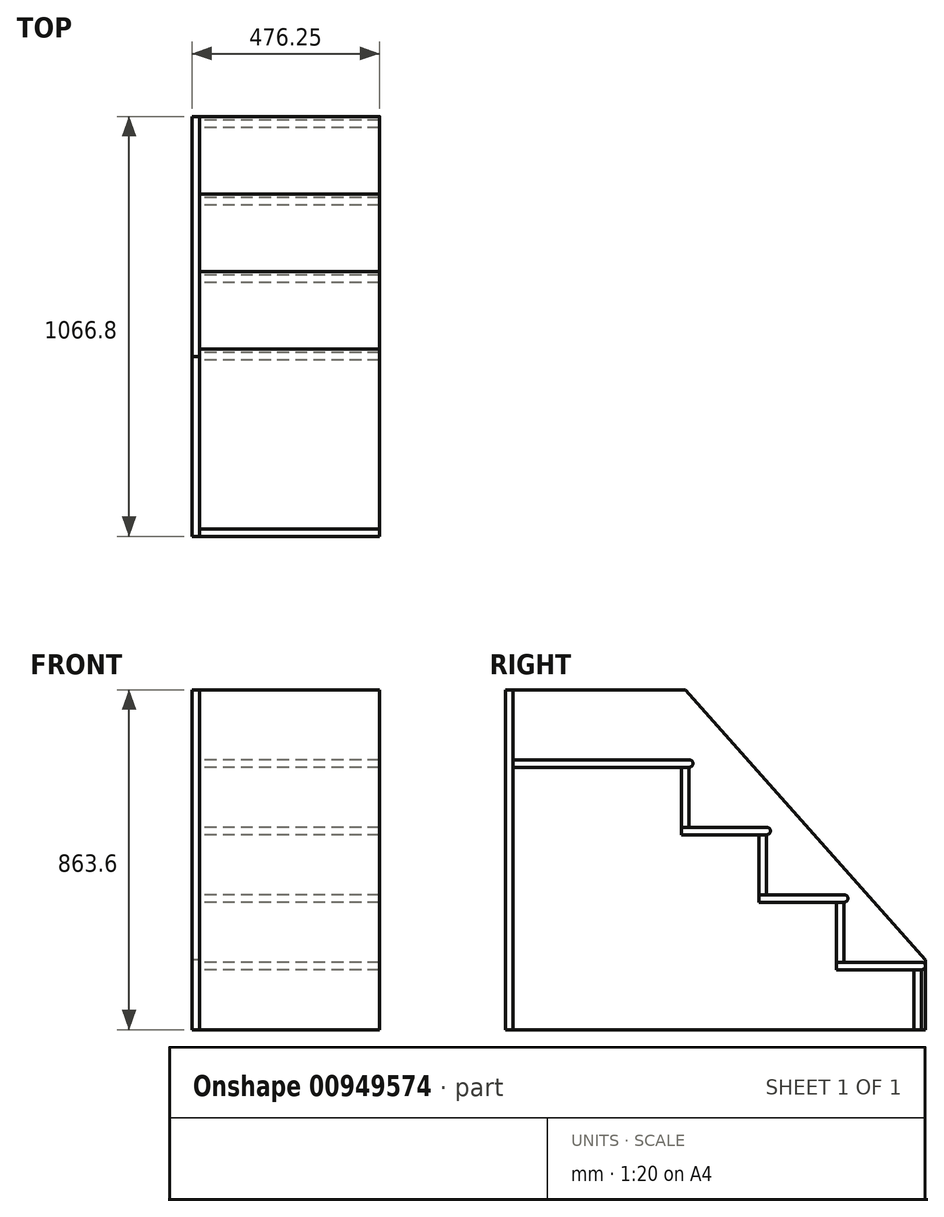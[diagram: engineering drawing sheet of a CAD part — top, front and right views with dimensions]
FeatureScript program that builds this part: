
annotation { "Feature Type Name" : "Feature", "Feature Type Description" : "" }
export const myFeature = defineFeature(function(context is Context, id is Id, definition is map)
    precondition{}
    {
        {
            var Q0;
            Q0=qCreatedBy(makeId("Right.planeOp"),FACE);
            var sketch = newSketch(context, id + "F0", { "sketchPlane" : qUnion([Q0])});
            skLineSegment(sketch, "E0", {"start": v(-1066.8, 863.6) * mm, "end": v(-1066.8, 0) * mm});
            skLineSegment(sketch, "E1", {"start": v(-1066.8, 0) * mm, "end": v(0, 0) * mm});
            skLineSegment(sketch, "E2", {"start": v(0, 0) * mm, "end": v(0, 177.8) * mm});
            skLineSegment(sketch, "E3", {"start": v(0, 177.8) * mm, "end": v(-609.6, 863.6) * mm});
            skLineSegment(sketch, "E4", {"start": v(-609.6, 863.6) * mm, "end": v(-1066.8, 863.6) * mm});
            skSolve(sketch);
        }
        {
            var Q0;
            Q0=makeQuery(id+"F0.imprint","IMPRINT",FACE,{"disambiguationData":[TD([[makeQuery(id+"F0.imprint","IMPRINT",EDGE,{"derivedFrom":sQuery(id+"F0.wireOp",EDGE,"E0")}),1.0]])]});
            extrude(context, id + "F1", {"entities" : qUnion([Q0]), "depth" : 19.05 * mm, "offsetDistance" : 25.4 * mm});
        }
        {
            var Q0;
            Q0=makeQuery(id+"F1.opExtrude","CAP_FACE",FACE,{"disambiguationData":[OSD([sQuery(id+"F0.wireOp",EDGE,"E0"),sQuery(id+"F0.wireOp",EDGE,"E1"),sQuery(id+"F0.wireOp",EDGE,"E2"),sQuery(id+"F0.wireOp",EDGE,"E3"),sQuery(id+"F0.wireOp",EDGE,"E4")])],"isStart":false});
            var sketch = newSketch(context, id + "F2", { "sketchPlane" : qUnion([Q0])});
            skLineSegment(sketch, "E5.bottom", {"start": v(-1047.75, 863.6) * mm, "end": v(-1066.8, 863.6) * mm});
            skLineSegment(sketch, "E5.top", {"start": v(-1047.75, 0) * mm, "end": v(-1066.8, 0) * mm});
            skLineSegment(sketch, "E5.left", {"start": v(-1047.75, 863.6) * mm, "end": v(-1047.75, 0) * mm});
            skLineSegment(sketch, "E5.right", {"start": v(-1066.8, 863.6) * mm, "end": v(-1066.8, 0) * mm});
            skSolve(sketch);
        }
        {
            var Q0;
            Q0 = qSketchRegion(id + "F2", true);
            extrude(context, id + "F3", {"entities" : qUnion([Q0]), "depth" : 457.2 * mm, "offsetDistance" : 25.4 * mm});
        }
        {
            var Q0;
            Q0=makeQuery(id+"F1.opExtrude","CAP_FACE",FACE,{"disambiguationData":[OSD([sQuery(id+"F0.wireOp",EDGE,"E0"),sQuery(id+"F0.wireOp",EDGE,"E1"),sQuery(id+"F0.wireOp",EDGE,"E2"),sQuery(id+"F0.wireOp",EDGE,"E3"),sQuery(id+"F0.wireOp",EDGE,"E4")])],"isStart":false});
            var sketch = newSketch(context, id + "F4", { "sketchPlane" : qUnion([Q0])});
            skLineSegment(sketch, "E6.bottom", {"start": v(-1047.75, 685.8) * mm, "end": v(-590.55, 685.8) * mm});
            skLineSegment(sketch, "E6.top", {"start": v(-1047.75, 666.75) * mm, "end": v(-590.55, 666.75) * mm});
            skLineSegment(sketch, "E6.left", {"start": v(-1047.75, 685.8) * mm, "end": v(-1047.75, 666.75) * mm});
            skLineSegment(sketch, "E6.right", {"start": v(-590.55, 685.8) * mm, "end": v(-590.55, 666.75) * mm});
            skLineSegment(sketch, "E7.bottom", {"start": v(-225.42, 171.45) * mm, "end": v(0, 171.45) * mm});
            skLineSegment(sketch, "E7.top", {"start": v(-225.42, 152.4) * mm, "end": v(0, 152.4) * mm});
            skLineSegment(sketch, "E7.left", {"start": v(-225.42, 171.45) * mm, "end": v(-225.42, 152.4) * mm});
            skLineSegment(sketch, "E7.right", {"start": v(0, 171.45) * mm, "end": v(0, 152.4) * mm});
            skLineSegment(sketch, "E8.bottom", {"start": v(-422.28, 342.9) * mm, "end": v(-196.85, 342.9) * mm});
            skLineSegment(sketch, "E8.top", {"start": v(-422.28, 323.85) * mm, "end": v(-196.85, 323.85) * mm});
            skLineSegment(sketch, "E8.left", {"start": v(-422.28, 342.9) * mm, "end": v(-422.28, 323.85) * mm});
            skLineSegment(sketch, "E8.right", {"start": v(-196.85, 342.9) * mm, "end": v(-196.85, 323.85) * mm});
            skLineSegment(sketch, "E9.bottom", {"start": v(-619.12, 514.35) * mm, "end": v(-393.7, 514.35) * mm});
            skLineSegment(sketch, "E9.top", {"start": v(-619.12, 495.3) * mm, "end": v(-393.7, 495.3) * mm});
            skLineSegment(sketch, "E9.left", {"start": v(-619.12, 514.35) * mm, "end": v(-619.12, 495.3) * mm});
            skLineSegment(sketch, "E9.right", {"start": v(-393.7, 514.35) * mm, "end": v(-393.7, 495.3) * mm});
            skSolve(sketch);
        }
        {
            var Q0;
            Q0 = qSketchRegion(id + "F4", true);
            var Q1;
            Q1=makeQuery(id+"F3.opExtrude","CAP_FACE",FACE,{"disambiguationData":[OSD([sQuery(id+"F2.wireOp",EDGE,"E5.bottom"),sQuery(id+"F2.wireOp",EDGE,"E5.top"),sQuery(id+"F2.wireOp",EDGE,"E5.left"),sQuery(id+"F2.wireOp",EDGE,"E5.right")])],"isStart":false});
            extrude(context, id + "F5", {"entities" : qUnion([Q0]), "endBound" : BoundingType.UP_TO_SURFACE, "depth" : 25.4 * mm, "endBoundEntityFace" : qUnion([Q1]), "offsetDistance" : 25.4 * mm});
        }
        {
            var Q0;
            Q0=makeQuery(id+"F5.opExtrude","SWEPT_EDGE",EDGE,{"disambiguationData":[OSD([sQuery(id+"F4.wireOp",EDGE,"E6.bottom"),sQuery(id+"F4.wireOp",EDGE,"E6.right")])]});
            var Q1;
            Q1=makeQuery(id+"F5.opExtrude","SWEPT_EDGE",EDGE,{"disambiguationData":[OSD([sQuery(id+"F4.wireOp",EDGE,"E6.top"),sQuery(id+"F4.wireOp",EDGE,"E6.right")])]});
            var Q2;
            Q2=makeQuery(id+"F5.opExtrude","SWEPT_EDGE",EDGE,{"disambiguationData":[OSD([sQuery(id+"F4.wireOp",EDGE,"E9.bottom"),sQuery(id+"F4.wireOp",EDGE,"E9.right")])]});
            var Q3;
            Q3=makeQuery(id+"F5.opExtrude","SWEPT_EDGE",EDGE,{"disambiguationData":[OSD([sQuery(id+"F4.wireOp",EDGE,"E9.top"),sQuery(id+"F4.wireOp",EDGE,"E9.right")])]});
            var Q4;
            Q4=makeQuery(id+"F5.opExtrude","SWEPT_EDGE",EDGE,{"disambiguationData":[OSD([sQuery(id+"F4.wireOp",EDGE,"E8.bottom"),sQuery(id+"F4.wireOp",EDGE,"E8.right")])]});
            var Q5;
            Q5=makeQuery(id+"F5.opExtrude","SWEPT_EDGE",EDGE,{"disambiguationData":[OSD([sQuery(id+"F4.wireOp",EDGE,"E8.top"),sQuery(id+"F4.wireOp",EDGE,"E8.right")])]});
            var Q6;
            Q6=makeQuery(id+"F5.opExtrude","SWEPT_EDGE",EDGE,{"disambiguationData":[OSD([sQuery(id+"F0.wireOp",EDGE,"E2"),sQuery(id+"F4.wireOp",EDGE,"E7.bottom"),sQuery(id+"F4.wireOp",EDGE,"E7.right")])]});
            var Q7;
            Q7=makeQuery(id+"F5.opExtrude","SWEPT_EDGE",EDGE,{"disambiguationData":[OSD([sQuery(id+"F0.wireOp",EDGE,"E2"),sQuery(id+"F4.wireOp",EDGE,"E7.top"),sQuery(id+"F4.wireOp",EDGE,"E7.right")])]});
            fillet(context, id + "F6", {"entities" : qUnion([Q0, Q1, Q2, Q3, Q4, Q5, Q6, Q7]), "radius" : 9.52 * mm, "tangentPropagation" : true, "allowEdgeOverflow" : false});
        }
        {
            var Q0;
            Q0=makeQuery(id+"F1.opExtrude","CAP_FACE",FACE,{"disambiguationData":[OSD([sQuery(id+"F0.wireOp",EDGE,"E0"),sQuery(id+"F0.wireOp",EDGE,"E1"),sQuery(id+"F0.wireOp",EDGE,"E2"),sQuery(id+"F0.wireOp",EDGE,"E3"),sQuery(id+"F0.wireOp",EDGE,"E4")])],"isStart":false});
            var sketch = newSketch(context, id + "F7", { "sketchPlane" : qUnion([Q0])});
            skLineSegment(sketch, "E10.bottom", {"start": v(-600.08, 666.75) * mm, "end": v(-619.12, 666.75) * mm});
            skLineSegment(sketch, "E10.top", {"start": v(-600.08, 514.35) * mm, "end": v(-619.12, 514.35) * mm});
            skLineSegment(sketch, "E10.left", {"start": v(-600.08, 666.75) * mm, "end": v(-600.08, 514.35) * mm});
            skLineSegment(sketch, "E10.right", {"start": v(-619.12, 666.75) * mm, "end": v(-619.12, 514.35) * mm});
            skLineSegment(sketch, "E11.bottom", {"start": v(-403.23, 495.3) * mm, "end": v(-422.28, 495.3) * mm});
            skLineSegment(sketch, "E11.top", {"start": v(-403.23, 342.9) * mm, "end": v(-422.28, 342.9) * mm});
            skLineSegment(sketch, "E11.left", {"start": v(-403.23, 495.3) * mm, "end": v(-403.23, 342.9) * mm});
            skLineSegment(sketch, "E11.right", {"start": v(-422.28, 495.3) * mm, "end": v(-422.28, 342.9) * mm});
            skLineSegment(sketch, "E12.bottom", {"start": v(-206.38, 323.85) * mm, "end": v(-225.43, 323.85) * mm});
            skLineSegment(sketch, "E12.top", {"start": v(-206.37, 171.45) * mm, "end": v(-225.42, 171.45) * mm});
            skLineSegment(sketch, "E12.left", {"start": v(-206.38, 323.85) * mm, "end": v(-206.37, 171.45) * mm});
            skLineSegment(sketch, "E12.right", {"start": v(-225.43, 323.85) * mm, "end": v(-225.42, 171.45) * mm});
            skLineSegment(sketch, "E13.bottom", {"start": v(-9.52, 152.4) * mm, "end": v(-28.57, 152.4) * mm});
            skLineSegment(sketch, "E13.top", {"start": v(-9.52, 0) * mm, "end": v(-28.57, 0) * mm});
            skLineSegment(sketch, "E13.left", {"start": v(-9.52, 152.4) * mm, "end": v(-9.52, 0) * mm});
            skLineSegment(sketch, "E13.right", {"start": v(-28.57, 152.4) * mm, "end": v(-28.57, 0) * mm});
            skSolve(sketch);
        }
        {
            var Q0;
            Q0 = qSketchRegion(id + "F7", true);
            var Q1;
            Q1=makeQuery(id+"F3.opExtrude","CAP_FACE",FACE,{"disambiguationData":[OSD([sQuery(id+"F2.wireOp",EDGE,"E5.bottom"),sQuery(id+"F2.wireOp",EDGE,"E5.top"),sQuery(id+"F2.wireOp",EDGE,"E5.left"),sQuery(id+"F2.wireOp",EDGE,"E5.right")])],"isStart":false});
            extrude(context, id + "F8", {"entities" : qUnion([Q0]), "endBound" : BoundingType.UP_TO_SURFACE, "depth" : 25.4 * mm, "endBoundEntityFace" : qUnion([Q1]), "offsetDistance" : 25.4 * mm});
        }
    });
